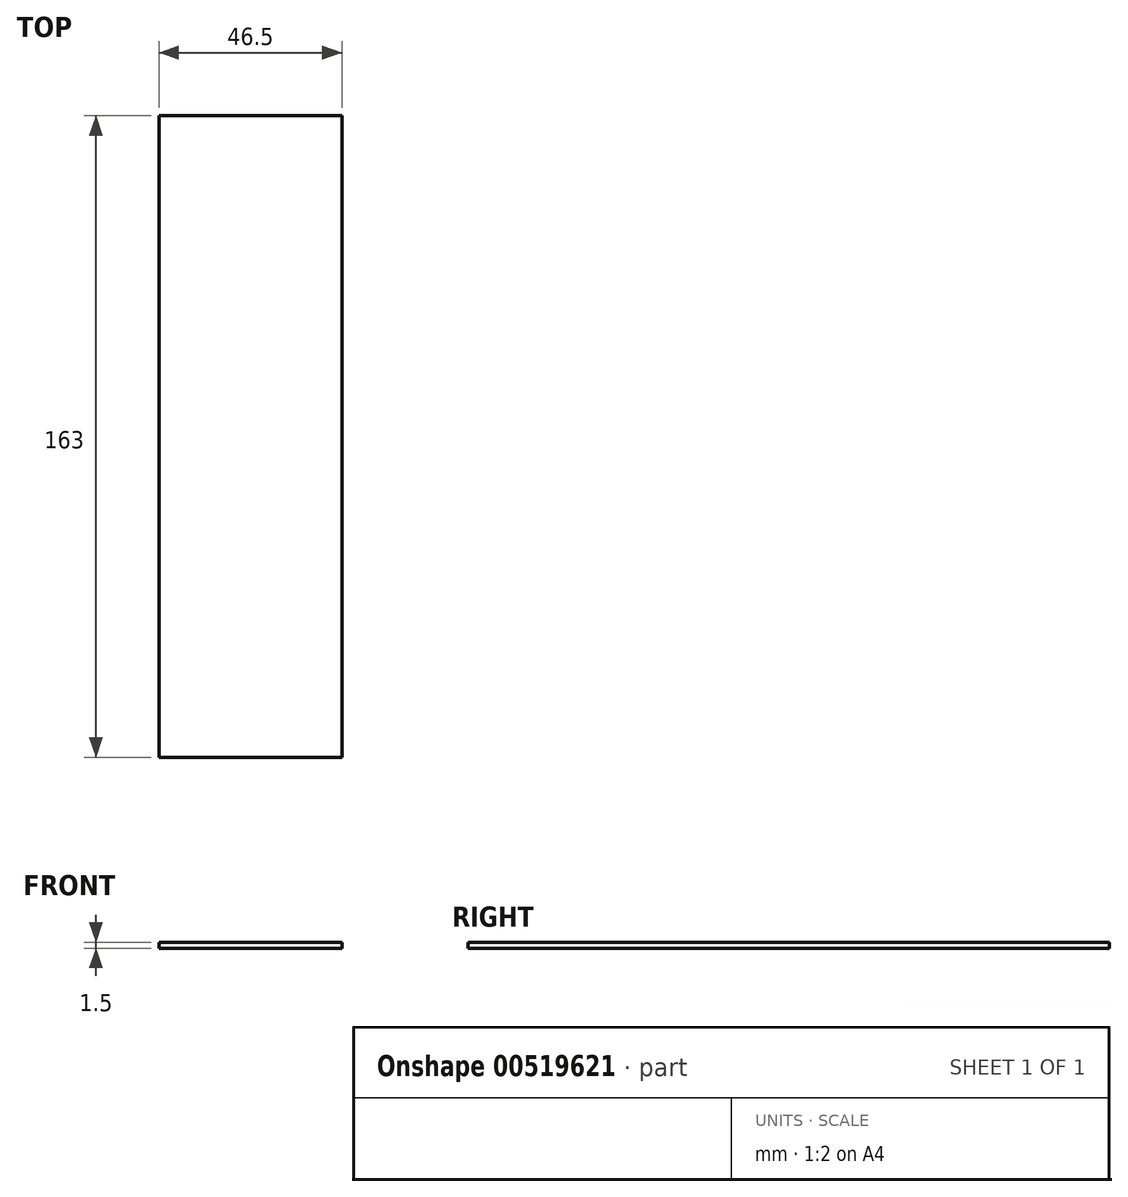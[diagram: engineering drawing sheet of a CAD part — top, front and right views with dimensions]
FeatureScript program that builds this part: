
annotation { "Feature Type Name" : "Feature", "Feature Type Description" : "" }
export const myFeature = defineFeature(function(context is Context, id is Id, definition is map)
    precondition{}
    {
        {
            var Q0;
            Q0=qCreatedBy(makeId("Top.planeOp"),FACE);
            var sketch = newSketch(context, id + "F0", { "sketchPlane" : qUnion([Q0])});
            skLineSegment(sketch, "E0.bottom", {"start": v(23.25, 81.5) * mm, "end": v(-23.25, 81.5) * mm});
            skLineSegment(sketch, "E0.top", {"start": v(23.25, -81.5) * mm, "end": v(-23.25, -81.5) * mm});
            skLineSegment(sketch, "E0.left", {"start": v(23.25, 81.5) * mm, "end": v(23.25, -81.5) * mm});
            skLineSegment(sketch, "E0.right", {"start": v(-23.25, 81.5) * mm, "end": v(-23.25, -81.5) * mm});
            skPoint(sketch, "E0.middle", {"position": v(0, 0) * mm});
            skSolve(sketch);
        }
        {
            var Q0;
            Q0 = qSketchRegion(id + "F0", true);
            extrude(context, id + "F1", {"entities" : qUnion([Q0]), "depth" : 1.5 * mm, "offsetDistance" : 25 * mm});
        }
    });
